# Revit family: MUTE_DESIGN_SPACE M
name_source: partatom
category: Modele ogólne
revit_build: Autodesk Revit 2017 (Build: 20160720_1515(x64)
units: mm (PartAtom-declared; Revit-internal decimal feet)

## family parameters
Może być obiektem nadrzędnym dla zbrojenia = Nie
Oparty na płaszczyźnie roboczej = Nie
Punkt obliczania pomieszczeń = Nie
Tnij formami wycięć po wczytaniu = Nie
Typ części = Normalny
Współdzielony = Nie
Wymiar okrągłego złącza = Użyj średnicy
Zawsze pionowo = Tak

## types (2) — shared parameters
Autor = www.archispace.pl
Filc = Mute_Design - Szary
Głębokość = 1000 mm  [stored 3.28084 ft]
Link do karty produktu = https://mutedesign.ovh
Link do strony produktu = https://mute.design
Materiał_blat = MUTE_DESIGN_domyślny
Materiał_hoker = MUTE_DESIGN_domyślny
Materiał_hoker_noga = Mute_Design - Rurka/klamka/noga_hoker - Szary
Materiał_klamka = Mute_Design - Rurka/klamka/noga_hoker - Szary
Materiał_przeszklenia = MUTE_DESIGN_Szkło
Materiał_rama = MUTE_DESIGN_domyślny
Materiał_ściany_i_dach = MUTE_DESIGN_domyślny
Model = SPACE S
Opis = Wysublimowana, ergonomiczna i funkcjonalna kabina Space S stworzy w Twoim biurze spokojne i kojące miejsce pracy, zapewniając Ci maksymalne skupienie na obowiązkach. To więcej niż zwykła budka. Technologia wbudowana w precyzyjnie zaprojektowaną konstrukcję kabiny Space S umożliwia swobodny kontakt ze światem zewnętrznym, bez rozpraszania przez jego codzienny rozgardiasz. Piękna forma i najlepsze właściwości akustyczne sprawiają, że kabina Space S jest symbiozą stylu, doskonałości wykonania i działania. Dzięki technologiom zastosowanym w budce Space S, takim jak port USB czy wbudowana ładowarka indukcyjna pozostaniesz w stałym kontakcie z otoczeniem. Kojące działanie budki Space S podkreślą drzwi i blaty, pokryte laminatem doskonale pasującym do metalowych ścian lub drewnem, które doda jej subtelnej elegancji. Efektywny system wentylacji w budce pozwoli Ci na długie telekonferencje. Zasiądź więc wygodnie na pięknie zaprojektowanym hokerze i delektuj się spokojem.
Producent = MuteDesign
Szerokość = 1000 mm  [stored 3.28084 ft]
URL = https://mute.design
Waga = 350.00 kg
Wysokość = 2247 mm  [stored 7.37205 ft]

## per-type parameters (varying)
| type | Blat | Blat_2 |
| Wersja 1osobowa | Tak | Nie |
| Wersja 2osobowa | Nie | Tak |

note: [stored X ft] marks values corroborated as IEEE doubles in the binary element streams (Revit-internal decimal feet)
